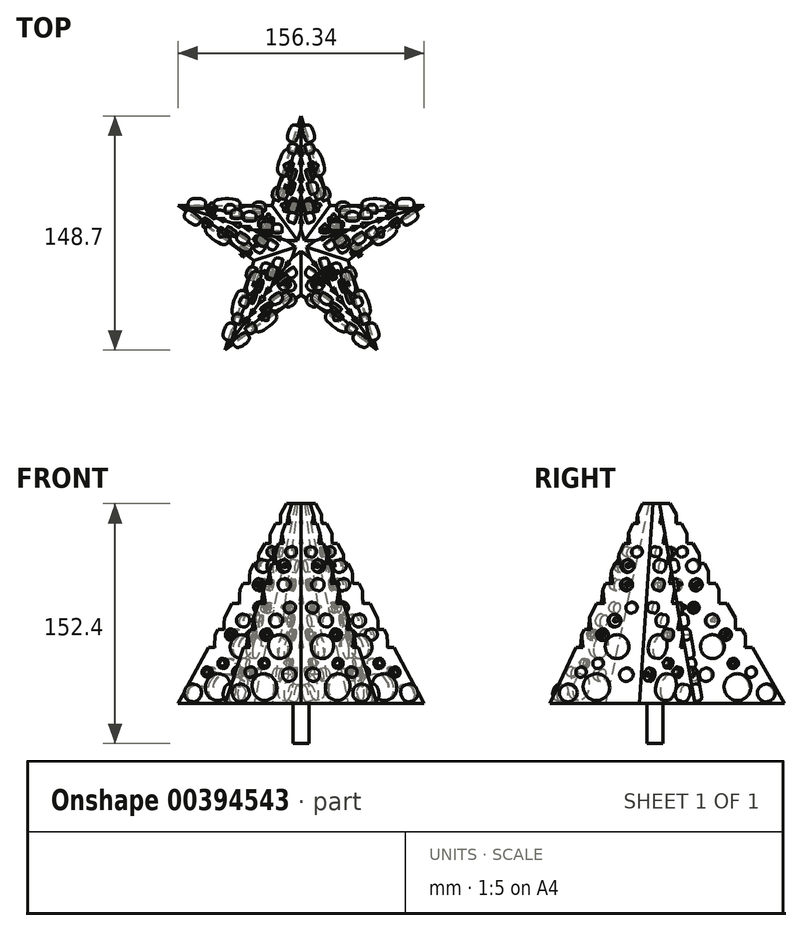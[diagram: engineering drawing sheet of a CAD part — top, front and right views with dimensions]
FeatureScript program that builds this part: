
annotation { "Feature Type Name" : "Feature", "Feature Type Description" : "" }
export const myFeature = defineFeature(function(context is Context, id is Id, definition is map)
    precondition{}
    {
        {
            var Q0;
            Q0=qCreatedBy(makeId("Top.planeOp"),FACE);
            var sketch = newSketch(context, id + "F0", { "sketchPlane" : qUnion([Q0])});
            skLineSegment(sketch, "E0", {"start": v(-78.17, 25.4) * mm, "end": v(48.31, -66.5) * mm});
            skLineSegment(sketch, "E1", {"start": v(48.31, -66.5) * mm, "end": v(0, 82.2) * mm});
            skLineSegment(sketch, "E2", {"start": v(0, 82.2) * mm, "end": v(-48.31, -66.5) * mm});
            skLineSegment(sketch, "E3", {"start": v(-48.31, -66.5) * mm, "end": v(78.17, 25.4) * mm});
            skLineSegment(sketch, "E4", {"start": v(78.17, 25.4) * mm, "end": v(-78.17, 25.4) * mm});
            skCircle(sketch, "E5.cCircle", {"center": v(0, 0) * mm, "radius": 25.4 * mm, "construction": true});
            skLineSegment(sketch, "E5.0", {"start": v(-29.86, -9.7) * mm, "end": v(-18.45, 25.4) * mm});
            skLineSegment(sketch, "E5.1", {"start": v(-18.45, 25.4) * mm, "end": v(18.45, 25.4) * mm});
            skLineSegment(sketch, "E5.2", {"start": v(18.45, 25.4) * mm, "end": v(29.86, -9.7) * mm});
            skLineSegment(sketch, "E5.3", {"start": v(29.86, -9.7) * mm, "end": v(0, -31.4) * mm});
            skLineSegment(sketch, "E5.4", {"start": v(0, -31.4) * mm, "end": v(-29.86, -9.7) * mm});
            skPoint(sketch, "E5.0.midPoint", {"position": v(-24.16, 7.85) * mm});
            skSolve(sketch);
        }
        {
            var Q0;
            Q0 = qSketchRegion(id + "F0", true);
            extrude(context, id + "F1", {"entities" : qUnion([Q0]), "depth" : 127 * mm, "hasDraft" : true, "draftAngle" : 10 * degree, "draftPullDirection" : true});
        }
        {
            var Q0;
            Q0=makeQuery(id+"F1.opExtrude","CAP_FACE",FACE,{"disambiguationData":[OSD([sQuery(id+"F0.wireOp",EDGE,"E0"),sQuery(id+"F0.wireOp",EDGE,"E1"),sQuery(id+"F0.wireOp",EDGE,"E2"),sQuery(id+"F0.wireOp",EDGE,"E3"),sQuery(id+"F0.wireOp",EDGE,"E4")])],"isStart":false});
            var sketch = newSketch(context, id + "F2", { "sketchPlane" : qUnion([Q0])});
            skCircle(sketch, "E6", {"center": v(0, 0) * mm, "radius": 13.59 * mm});
            skCircle(sketch, "E7", {"center": v(0, 0) * mm, "radius": 17.47 * mm});
            skCircle(sketch, "E8", {"center": v(0, 0) * mm, "radius": 20.54 * mm});
            skCircle(sketch, "E9", {"center": v(0, 0) * mm, "radius": 24.38 * mm});
            skCircle(sketch, "E10", {"center": v(0, 0) * mm, "radius": 28.24 * mm});
            skCircle(sketch, "E11", {"center": v(0, 0) * mm, "radius": 34.11 * mm});
            skCircle(sketch, "E12", {"center": v(0, 0) * mm, "radius": 40.82 * mm});
            skCircle(sketch, "E13", {"center": v(0, 0) * mm, "radius": 46.28 * mm});
            skCircle(sketch, "E14", {"center": v(0, 0) * mm, "radius": 51.14 * mm});
            skCircle(sketch, "E15", {"center": v(0, 0) * mm, "radius": 57.41 * mm});
            skCircle(sketch, "E16", {"center": v(0, 0) * mm, "radius": 65.5 * mm});
            skSolve(sketch);
        }
        {
            var Q0;
            Q0=makeQuery(id+"F2.imprint","IMPRINT",FACE,{"disambiguationData":[TD([[makeQuery(id+"F2.imprint","IMPRINT",EDGE,{"derivedFrom":sQuery(id+"F2.wireOp",EDGE,"E6")}),-1.0]])]});
            extrude(context, id + "F3", {"entities" : qUnion([Q0]), "operationType" : NewBodyOperationType.REMOVE, "oppositeDirection" : true, "depth" : 12.7 * mm});
        }
        {
            var Q0;
            Q0=makeQuery(id+"F2.imprint","IMPRINT",FACE,{"disambiguationData":[TD([[makeQuery(id+"F2.imprint","IMPRINT",EDGE,{"derivedFrom":sQuery(id+"F2.wireOp",EDGE,"E8")}),-1.0]])]});
            extrude(context, id + "F4", {"entities" : qUnion([Q0]), "operationType" : NewBodyOperationType.REMOVE, "oppositeDirection" : true, "depth" : 25.4 * mm});
        }
        {
            var Q0;
            Q0=makeQuery(id+"F2.imprint","IMPRINT",FACE,{"disambiguationData":[TD([[makeQuery(id+"F2.imprint","IMPRINT",EDGE,{"derivedFrom":sQuery(id+"F2.wireOp",EDGE,"E10")}),-1.0]])]});
            extrude(context, id + "F5", {"entities" : qUnion([Q0]), "operationType" : NewBodyOperationType.REMOVE, "oppositeDirection" : true, "depth" : 38.1 * mm});
        }
        {
            var Q0;
            Q0=makeQuery(id+"F2.imprint","IMPRINT",FACE,{"disambiguationData":[TD([[makeQuery(id+"F2.imprint","IMPRINT",EDGE,{"derivedFrom":sQuery(id+"F2.wireOp",EDGE,"E11")}),-1.0]])]});
            extrude(context, id + "F6", {"entities" : qUnion([Q0]), "operationType" : NewBodyOperationType.REMOVE, "oppositeDirection" : true, "depth" : 50.8 * mm});
        }
        {
            var Q0;
            Q0=makeQuery(id+"F2.imprint","IMPRINT",FACE,{"disambiguationData":[TD([[makeQuery(id+"F2.imprint","IMPRINT",EDGE,{"derivedFrom":sQuery(id+"F2.wireOp",EDGE,"E12")}),-1.0]])]});
            extrude(context, id + "F7", {"entities" : qUnion([Q0]), "operationType" : NewBodyOperationType.REMOVE, "oppositeDirection" : true, "depth" : 63.5 * mm});
        }
        {
            var Q0;
            Q0=makeQuery(id+"F2.imprint","IMPRINT",FACE,{"disambiguationData":[TD([[makeQuery(id+"F2.imprint","IMPRINT",EDGE,{"derivedFrom":sQuery(id+"F2.wireOp",EDGE,"E14")}),-1.0]])]});
            extrude(context, id + "F8", {"entities" : qUnion([Q0]), "operationType" : NewBodyOperationType.REMOVE, "oppositeDirection" : true, "depth" : 80 * mm});
        }
        {
            var Q0;
            Q0=makeQuery(id+"F2.imprint","IMPRINT",FACE,{"disambiguationData":[TD([[makeQuery(id+"F2.imprint","IMPRINT",EDGE,{"derivedFrom":sQuery(id+"F2.wireOp",EDGE,"E15")}),-1.0]])]});
            extrude(context, id + "F9", {"entities" : qUnion([Q0]), "operationType" : NewBodyOperationType.REMOVE, "oppositeDirection" : true, "depth" : 91.44 * mm});
        }
        {
            var Q0;
            {var subQ0=sQuery(id+"F0.wireOp",EDGE,"E0");Q0=makeQuery(id+"F1.opExtrude","SWEPT_FACE",FACE,{"disambiguationData":[OSD([subQ0]),TDD([makeQuery(id+"F0.imprint","IMPRINT",EDGE,{"disambiguationData":[TD([[makeQuery(id+"F0.imprint","INTERSECT",VERTEX,{"derivedFrom":[subQ0,sQuery(id+"F0.wireOp",EDGE,"E1")]}),1.0]])],"derivedFrom":subQ0})])]});}
            var sketch = newSketch(context, id + "F10", { "sketchPlane" : qUnion([Q0])});
            skCircle(sketch, "E17", {"center": v(26.64, 90.5) * mm, "radius": 3.16 * mm});
            skCircle(sketch, "E18", {"center": v(32.05, 68.5) * mm, "radius": 3.7 * mm});
            skCircle(sketch, "E19", {"center": v(32.23, 80.66) * mm, "radius": 3.94 * mm});
            skCircle(sketch, "E20", {"center": v(45.73, 34.3) * mm, "radius": 3.54 * mm});
            skCircle(sketch, "E21", {"center": v(38.43, 44.36) * mm, "radius": 3.95 * mm});
            skCircle(sketch, "E22", {"center": v(27.73, 54.12) * mm, "radius": 3.33 * mm});
            skCircle(sketch, "E23", {"center": v(35.59, 27.8) * mm, "radius": 7.5 * mm});
            skCircle(sketch, "E24", {"center": v(58.31, 8.36) * mm, "radius": 3.13 * mm});
            skCircle(sketch, "E25", {"center": v(47.46, 0) * mm, "radius": 8.43 * mm});
            skCircle(sketch, "E26", {"center": v(65.9, -6.12) * mm, "radius": 5.5 * mm});
            skCircle(sketch, "E27", {"center": v(28.18, 10.48) * mm, "radius": 4.1 * mm});
            skCircle(sketch, "E28", {"center": v(47.46, 15.43) * mm, "radius": 3.12 * mm});
            skSolve(sketch);
        }
        {
            var Q0;
            Q0 = qSketchRegion(id + "F10", true);
            extrude(context, id + "F11", {"entities" : qUnion([Q0]), "depth" : 5.08 * mm});
        }
        {
            var Q0;
            Q0=makeQuery(id+"F11.opExtrude","CAP_EDGE",EDGE,{"disambiguationData":[OSD([sQuery(id+"F10.wireOp",EDGE,"E17")])],"isStart":false});
            var Q1;
            Q1=makeQuery(id+"F11.opExtrude","CAP_EDGE",EDGE,{"disambiguationData":[OSD([sQuery(id+"F10.wireOp",EDGE,"E23")])],"isStart":false});
            var Q2;
            Q2=makeQuery(id+"F11.opExtrude","CAP_EDGE",EDGE,{"disambiguationData":[OSD([sQuery(id+"F10.wireOp",EDGE,"E28")])],"isStart":false});
            var Q3;
            Q3=makeQuery(id+"F11.opExtrude","CAP_EDGE",EDGE,{"disambiguationData":[OSD([sQuery(id+"F10.wireOp",EDGE,"E25")])],"isStart":false});
            var Q4;
            Q4=makeQuery(id+"F11.opExtrude","CAP_EDGE",EDGE,{"disambiguationData":[OSD([sQuery(id+"F10.wireOp",EDGE,"E27")])],"isStart":false});
            var Q5;
            Q5=makeQuery(id+"F11.opExtrude","CAP_EDGE",EDGE,{"disambiguationData":[OSD([sQuery(id+"F10.wireOp",EDGE,"E26")])],"isStart":false});
            var Q6;
            Q6=makeQuery(id+"F11.opExtrude","CAP_EDGE",EDGE,{"disambiguationData":[OSD([sQuery(id+"F10.wireOp",EDGE,"E24")])],"isStart":false});
            var Q7;
            Q7=makeQuery(id+"F11.opExtrude","CAP_EDGE",EDGE,{"disambiguationData":[OSD([sQuery(id+"F10.wireOp",EDGE,"E20")])],"isStart":false});
            var Q8;
            Q8=makeQuery(id+"F11.opExtrude","CAP_EDGE",EDGE,{"disambiguationData":[OSD([sQuery(id+"F10.wireOp",EDGE,"E21")])],"isStart":false});
            var Q9;
            Q9=makeQuery(id+"F11.opExtrude","CAP_EDGE",EDGE,{"disambiguationData":[OSD([sQuery(id+"F10.wireOp",EDGE,"E22")])],"isStart":false});
            var Q10;
            Q10=makeQuery(id+"F11.opExtrude","CAP_EDGE",EDGE,{"disambiguationData":[OSD([sQuery(id+"F10.wireOp",EDGE,"E18")])],"isStart":false});
            var Q11;
            Q11=makeQuery(id+"F11.opExtrude","CAP_EDGE",EDGE,{"disambiguationData":[OSD([sQuery(id+"F10.wireOp",EDGE,"E19")])],"isStart":false});
            fillet(context, id + "F12", {"entities" : qUnion([Q0, Q1, Q2, Q3, Q4, Q5, Q6, Q7, Q8, Q9, Q10, Q11]), "radius" : 2.54 * mm, "tangentPropagation" : true, "allowEdgeOverflow" : false});
        }
        {
            var Q0;
            Q0=makeQuery(id+"F11.opExtrude","SWEPT_BODY",BODY,{"disambiguationData":[OSD([sQuery(id+"F10.wireOp",EDGE,"E17")])]});
            var Q1;
            Q1=makeQuery(id+"F11.opExtrude","SWEPT_BODY",BODY,{"disambiguationData":[OSD([sQuery(id+"F10.wireOp",EDGE,"E18")])]});
            var Q2;
            Q2=makeQuery(id+"F11.opExtrude","SWEPT_BODY",BODY,{"disambiguationData":[OSD([sQuery(id+"F10.wireOp",EDGE,"E19")])]});
            var Q3;
            Q3=makeQuery(id+"F11.opExtrude","SWEPT_BODY",BODY,{"disambiguationData":[OSD([sQuery(id+"F10.wireOp",EDGE,"E20")])]});
            var Q4;
            Q4=makeQuery(id+"F11.opExtrude","SWEPT_BODY",BODY,{"disambiguationData":[OSD([sQuery(id+"F10.wireOp",EDGE,"E21")])]});
            var Q5;
            Q5=makeQuery(id+"F11.opExtrude","SWEPT_BODY",BODY,{"disambiguationData":[OSD([sQuery(id+"F10.wireOp",EDGE,"E22")])]});
            var Q6;
            Q6=makeQuery(id+"F11.opExtrude","SWEPT_BODY",BODY,{"disambiguationData":[OSD([sQuery(id+"F10.wireOp",EDGE,"E23")])]});
            var Q7;
            Q7=makeQuery(id+"F11.opExtrude","SWEPT_BODY",BODY,{"disambiguationData":[OSD([sQuery(id+"F10.wireOp",EDGE,"E24")])]});
            var Q8;
            Q8=makeQuery(id+"F11.opExtrude","SWEPT_BODY",BODY,{"disambiguationData":[OSD([sQuery(id+"F10.wireOp",EDGE,"E25")])]});
            var Q9;
            Q9=makeQuery(id+"F11.opExtrude","SWEPT_BODY",BODY,{"disambiguationData":[OSD([sQuery(id+"F10.wireOp",EDGE,"E26")])]});
            var Q10;
            Q10=makeQuery(id+"F11.opExtrude","SWEPT_BODY",BODY,{"disambiguationData":[OSD([sQuery(id+"F10.wireOp",EDGE,"E27")])]});
            var Q11;
            Q11=makeQuery(id+"F11.opExtrude","SWEPT_BODY",BODY,{"disambiguationData":[OSD([sQuery(id+"F10.wireOp",EDGE,"E28")])]});
            var Q12;
            Q12=sQuery(id+"F2.wireOp",EDGE,"E16");
            circularPattern(context, id + "F13", {"entities" : qUnion([Q0, Q1, Q2, Q3, Q4, Q5, Q6, Q7, Q8, Q9, Q10, Q11]), "axis" : qUnion([Q12]), "angle" : 360 * degree, "instanceCount" : 5, "equalSpace" : true});
        }
        {
            var Q0;
            Q0=makeQuery(id+"F13.opPattern","COPY",BODY,{"derivedFrom":makeQuery(id+"F11.opExtrude","SWEPT_BODY",BODY,{"disambiguationData":[OSD([sQuery(id+"F10.wireOp",EDGE,"E17")])]}),"instanceName":"2"});
            var Q1;
            Q1=makeQuery(id+"F13.opPattern","COPY",BODY,{"derivedFrom":makeQuery(id+"F11.opExtrude","SWEPT_BODY",BODY,{"disambiguationData":[OSD([sQuery(id+"F10.wireOp",EDGE,"E19")])]}),"instanceName":"2"});
            var Q2;
            Q2=makeQuery(id+"F13.opPattern","COPY",BODY,{"derivedFrom":makeQuery(id+"F11.opExtrude","SWEPT_BODY",BODY,{"disambiguationData":[OSD([sQuery(id+"F10.wireOp",EDGE,"E18")])]}),"instanceName":"2"});
            var Q3;
            Q3=makeQuery(id+"F13.opPattern","COPY",BODY,{"derivedFrom":makeQuery(id+"F11.opExtrude","SWEPT_BODY",BODY,{"disambiguationData":[OSD([sQuery(id+"F10.wireOp",EDGE,"E22")])]}),"instanceName":"2"});
            var Q4;
            Q4=makeQuery(id+"F13.opPattern","COPY",BODY,{"derivedFrom":makeQuery(id+"F11.opExtrude","SWEPT_BODY",BODY,{"disambiguationData":[OSD([sQuery(id+"F10.wireOp",EDGE,"E21")])]}),"instanceName":"2"});
            var Q5;
            Q5=makeQuery(id+"F13.opPattern","COPY",BODY,{"derivedFrom":makeQuery(id+"F11.opExtrude","SWEPT_BODY",BODY,{"disambiguationData":[OSD([sQuery(id+"F10.wireOp",EDGE,"E20")])]}),"instanceName":"2"});
            var Q6;
            Q6=makeQuery(id+"F13.opPattern","COPY",BODY,{"derivedFrom":makeQuery(id+"F11.opExtrude","SWEPT_BODY",BODY,{"disambiguationData":[OSD([sQuery(id+"F10.wireOp",EDGE,"E23")])]}),"instanceName":"2"});
            var Q7;
            Q7=makeQuery(id+"F13.opPattern","COPY",BODY,{"derivedFrom":makeQuery(id+"F11.opExtrude","SWEPT_BODY",BODY,{"disambiguationData":[OSD([sQuery(id+"F10.wireOp",EDGE,"E27")])]}),"instanceName":"2"});
            var Q8;
            Q8=makeQuery(id+"F13.opPattern","COPY",BODY,{"derivedFrom":makeQuery(id+"F11.opExtrude","SWEPT_BODY",BODY,{"disambiguationData":[OSD([sQuery(id+"F10.wireOp",EDGE,"E28")])]}),"instanceName":"2"});
            var Q9;
            Q9=makeQuery(id+"F13.opPattern","COPY",BODY,{"derivedFrom":makeQuery(id+"F11.opExtrude","SWEPT_BODY",BODY,{"disambiguationData":[OSD([sQuery(id+"F10.wireOp",EDGE,"E24")])]}),"instanceName":"2"});
            var Q10;
            Q10=makeQuery(id+"F13.opPattern","COPY",BODY,{"derivedFrom":makeQuery(id+"F11.opExtrude","SWEPT_BODY",BODY,{"disambiguationData":[OSD([sQuery(id+"F10.wireOp",EDGE,"E26")])]}),"instanceName":"2"});
            var Q11;
            Q11=makeQuery(id+"F13.opPattern","COPY",BODY,{"derivedFrom":makeQuery(id+"F11.opExtrude","SWEPT_BODY",BODY,{"disambiguationData":[OSD([sQuery(id+"F10.wireOp",EDGE,"E25")])]}),"instanceName":"2"});
            var Q12;
            Q12=qCreatedBy(makeId("Right.planeOp"),FACE);
            mirror(context, id + "F14", {"entities" : qUnion([Q0, Q1, Q2, Q3, Q4, Q5, Q6, Q7, Q8, Q9, Q10, Q11]), "mirrorPlane" : qUnion([Q12])});
        }
        {
            var Q0;
            Q0=makeQuery(id+"F14.opPattern","COPY",BODY,{"derivedFrom":makeQuery(id+"F13.opPattern","COPY",BODY,{"derivedFrom":makeQuery(id+"F11.opExtrude","SWEPT_BODY",BODY,{"disambiguationData":[OSD([sQuery(id+"F10.wireOp",EDGE,"E17")])]}),"instanceName":"2"}),"instanceName":"1"});
            var Q1;
            Q1=makeQuery(id+"F14.opPattern","COPY",BODY,{"derivedFrom":makeQuery(id+"F13.opPattern","COPY",BODY,{"derivedFrom":makeQuery(id+"F11.opExtrude","SWEPT_BODY",BODY,{"disambiguationData":[OSD([sQuery(id+"F10.wireOp",EDGE,"E19")])]}),"instanceName":"2"}),"instanceName":"1"});
            var Q2;
            Q2=makeQuery(id+"F14.opPattern","COPY",BODY,{"derivedFrom":makeQuery(id+"F13.opPattern","COPY",BODY,{"derivedFrom":makeQuery(id+"F11.opExtrude","SWEPT_BODY",BODY,{"disambiguationData":[OSD([sQuery(id+"F10.wireOp",EDGE,"E18")])]}),"instanceName":"2"}),"instanceName":"1"});
            var Q3;
            Q3=makeQuery(id+"F14.opPattern","COPY",BODY,{"derivedFrom":makeQuery(id+"F13.opPattern","COPY",BODY,{"derivedFrom":makeQuery(id+"F11.opExtrude","SWEPT_BODY",BODY,{"disambiguationData":[OSD([sQuery(id+"F10.wireOp",EDGE,"E22")])]}),"instanceName":"2"}),"instanceName":"1"});
            var Q4;
            Q4=makeQuery(id+"F14.opPattern","COPY",BODY,{"derivedFrom":makeQuery(id+"F13.opPattern","COPY",BODY,{"derivedFrom":makeQuery(id+"F11.opExtrude","SWEPT_BODY",BODY,{"disambiguationData":[OSD([sQuery(id+"F10.wireOp",EDGE,"E23")])]}),"instanceName":"2"}),"instanceName":"1"});
            var Q5;
            Q5=makeQuery(id+"F14.opPattern","COPY",BODY,{"derivedFrom":makeQuery(id+"F13.opPattern","COPY",BODY,{"derivedFrom":makeQuery(id+"F11.opExtrude","SWEPT_BODY",BODY,{"disambiguationData":[OSD([sQuery(id+"F10.wireOp",EDGE,"E21")])]}),"instanceName":"2"}),"instanceName":"1"});
            var Q6;
            Q6=makeQuery(id+"F14.opPattern","COPY",BODY,{"derivedFrom":makeQuery(id+"F13.opPattern","COPY",BODY,{"derivedFrom":makeQuery(id+"F11.opExtrude","SWEPT_BODY",BODY,{"disambiguationData":[OSD([sQuery(id+"F10.wireOp",EDGE,"E20")])]}),"instanceName":"2"}),"instanceName":"1"});
            var Q7;
            Q7=makeQuery(id+"F14.opPattern","COPY",BODY,{"derivedFrom":makeQuery(id+"F13.opPattern","COPY",BODY,{"derivedFrom":makeQuery(id+"F11.opExtrude","SWEPT_BODY",BODY,{"disambiguationData":[OSD([sQuery(id+"F10.wireOp",EDGE,"E28")])]}),"instanceName":"2"}),"instanceName":"1"});
            var Q8;
            Q8=makeQuery(id+"F14.opPattern","COPY",BODY,{"derivedFrom":makeQuery(id+"F13.opPattern","COPY",BODY,{"derivedFrom":makeQuery(id+"F11.opExtrude","SWEPT_BODY",BODY,{"disambiguationData":[OSD([sQuery(id+"F10.wireOp",EDGE,"E27")])]}),"instanceName":"2"}),"instanceName":"1"});
            var Q9;
            Q9=makeQuery(id+"F14.opPattern","COPY",BODY,{"derivedFrom":makeQuery(id+"F13.opPattern","COPY",BODY,{"derivedFrom":makeQuery(id+"F11.opExtrude","SWEPT_BODY",BODY,{"disambiguationData":[OSD([sQuery(id+"F10.wireOp",EDGE,"E25")])]}),"instanceName":"2"}),"instanceName":"1"});
            var Q10;
            Q10=makeQuery(id+"F14.opPattern","COPY",BODY,{"derivedFrom":makeQuery(id+"F13.opPattern","COPY",BODY,{"derivedFrom":makeQuery(id+"F11.opExtrude","SWEPT_BODY",BODY,{"disambiguationData":[OSD([sQuery(id+"F10.wireOp",EDGE,"E24")])]}),"instanceName":"2"}),"instanceName":"1"});
            var Q11;
            Q11=makeQuery(id+"F14.opPattern","COPY",BODY,{"derivedFrom":makeQuery(id+"F13.opPattern","COPY",BODY,{"derivedFrom":makeQuery(id+"F11.opExtrude","SWEPT_BODY",BODY,{"disambiguationData":[OSD([sQuery(id+"F10.wireOp",EDGE,"E26")])]}),"instanceName":"2"}),"instanceName":"1"});
            var Q12;
            Q12=sQuery(id+"F2.wireOp",EDGE,"E8");
            circularPattern(context, id + "F15", {"entities" : qUnion([Q0, Q1, Q2, Q3, Q4, Q5, Q6, Q7, Q8, Q9, Q10, Q11]), "axis" : qUnion([Q12]), "angle" : 360 * degree, "instanceCount" : 5, "equalSpace" : true});
        }
        {
            var Q0;
            Q0=makeQuery(id+"F1.opExtrude","CAP_FACE",FACE,{"disambiguationData":[OSD([sQuery(id+"F0.wireOp",EDGE,"E0"),sQuery(id+"F0.wireOp",EDGE,"E1"),sQuery(id+"F0.wireOp",EDGE,"E2"),sQuery(id+"F0.wireOp",EDGE,"E3"),sQuery(id+"F0.wireOp",EDGE,"E4")])],"isStart":true});
            var sketch = newSketch(context, id + "F16", { "sketchPlane" : qUnion([Q0])});
            skCircle(sketch, "E29", {"center": v(0, 0) * mm, "radius": 5.06 * mm});
            skSolve(sketch);
        }
        {
            var Q0;
            Q0 = qSketchRegion(id + "F16", true);
            extrude(context, id + "F17", {"entities" : qUnion([Q0]), "depth" : 25.4 * mm});
        }
    });
